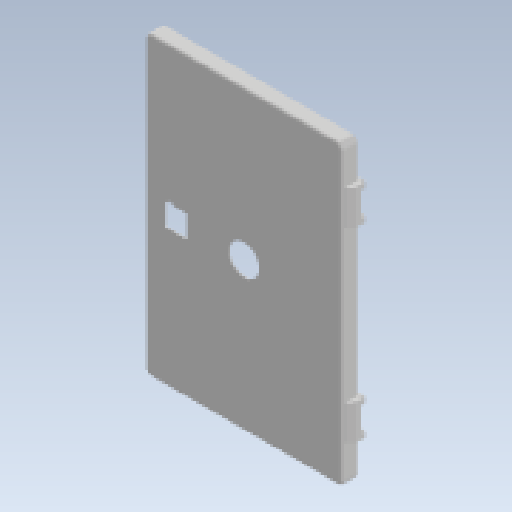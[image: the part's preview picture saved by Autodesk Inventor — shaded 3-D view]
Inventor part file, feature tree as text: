
AUTODESK INVENTOR PART (.ipt)
format: ipt  version: 2025.2 (Build 292293000, 293)  size: 422,400 bytes
history: native  units: mm
features: other x28, sketch x22, extrude x14, revolve x9, thread x1
ambient origin geometry x8: Origin, YZ Plane, XZ Plane, XY Plane, X Axis, Y Axis, Z Axis, Center Point
bodies: Solid1 (feature_tree)
feature tree (74):
  extrude  "Extrusion1"  Depth=286.0mm TaperAngle=0.0deg
  extrude  "Extrusion2"  TaperAngle=90.0deg  [1 undecoded]
  revolve  "Revolution1"  Angle=90.0deg
  revolve  "Revolution2"  Angle=90.0deg
  revolve  "Revolution3"  Angle=90.0deg
  revolve  "Revolution4"  [1 undecoded]
  extrude  "Extrusion3"  Depth=188.0mm TaperAngle=0.0deg
  revolve  "Revolution5"  Angle=360.0deg
  revolve  "Revolution6"  [1 undecoded]
  revolve  "Revolution7"  [1 undecoded]
  revolve  "Revolution8"  [1 undecoded]
  extrude  "Extrusion4"  Depth=30.52mm
  extrude  "Extrusion5"  Depth=10.0mm
  extrude  "Extrusion6"  Depth=30.02mm
  extrude  "Extrusion7"  Depth=10.0mm TaperAngle=0.0deg
  revolve  "Revolution9"  [1 undecoded]
  thread  "Thread1"  [1 undecoded]
  extrude  "Extrusion8"  [1 undecoded]
  extrude  "Extrusion9"  [1 undecoded]
  extrude  "Extrusion10"  [1 undecoded]
  extrude  "Extrusion11"  [1 undecoded]
  other  "DECKEL_XY"
  other  "DECKEL_YZ"
  other  "DECKEL_ZX"
  other  "DECKEL_X"
  other  "DECKEL_Y"
  other  "DECKEL_Z"
  other  "DECKEL_Center"
  other  "VB_XY"
  other  "VB_YZ"
  other  "VB_ZX"
  other  "VB_X"
  other  "VB_Y"
  other  "VB_Z"
  other  "VB_Center"
  other  "to_HINGE_XY"
  other  "to_HINGE_YZ"
  other  "to_HINGE_ZX"
  other  "to_HINGE_X"
  other  "to_HINGE_Y"
  other  "to_HINGE_Z"
  other  "to_HINGE_Center"
  other  "to_HINGE_1_XY"
  other  "to_HINGE_1_YZ"
  other  "to_HINGE_1_ZX"
  other  "to_HINGE_1_X"
  other  "to_HINGE_1_Y"
  other  "to_HINGE_1_Z"
  other  "to_HINGE_1_Center"
  extrude  "Extrusão12"  [1 undecoded]
  sketch  "Esboço22"  dims[d44=10.0mm d45=0.0mm]
  extrude  "Extrusão13"  [1 undecoded]
  extrude  "Extrusão14"  [1 undecoded]
  sketch  "Skizze_2"  dims[d4=90.0deg d5=90.0deg]
  sketch  "Skizze_4"  dims[d8=176.5mm d9=0.0mm d10=90.0deg]
  sketch  "Skizze_5"  dims[d13=90.0deg d14=276.5mm d15=0.0mm]
  sketch  "Skizze_6"  dims[d20=1.25mm d21=0.0mm d22=360.0deg]
  sketch  "Skizze_7"  dims[d27=35.0mm d28=0.0mm d29=25.0mm d30=0.0mm]
  sketch  "Skizze_8"  dims[d31=25.0mm d32=0.0mm d33=0.0mm]
  sketch  "Skizze_29"
  sketch  "Skizze_30"
  sketch  "Skizze_31"
  sketch  "Skizze_32"
  sketch  "Skizze_33"
  sketch  "Skizze_34"
  sketch  "Sketch_5"  dims[d16=288.0mm d17=0.0mm d18=188.0mm d19=0.0mm]
  sketch  "Sketch_6"  dims[d23=7.1865mm d24=0.0mm d25=35.0mm d26=0.0mm]
  sketch  "Sketch_3"  dims[d6=90.0deg d7=90.0deg]
  sketch  "Sketch_1"  dims[d0=186.0mm d1=0.0mm d2=286.0mm d3=0.0mm]
  sketch  "Sketch_4"  dims[d11=90.0deg d12=90.0deg]
  sketch  "Sketch_10"  dims[d36=10.0mm d37=0.0mm d38=70.0mm]
  sketch  "Sketch_9"  dims[d34=0.0mm d35=30.52mm]
  sketch  "Sketch_11"  dims[d39=50.0mm d40=30.02mm]
  sketch  "Esboço21"  dims[d41=50.0mm d42=10.0mm d43=0.0mm]
note: 14 required parameter values undecoded (feature->parameter linkage not recoverable at this tier; creation-order binding heuristic only, values carry confidence <= 0.55)